# Revit family: HVAC_Water-Heaters_Enertech_CTC-EcoAir-510M
name_source: partatom
category: Specialty Equipment
revit_build: Autodesk Revit 2017 (Build: 20190508_0315(x64)
units: mm (PartAtom-declared; Revit-internal decimal feet)

## family parameters
Always vertical = Yes
Cut with Voids When Loaded = No
OmniClass Number = 23.75.00.00
OmniClass Title = Climate Control (HVAC)
Part Type = Normal
Room Calculation Point = No
Round Connector Dimension = Use Diameter
Shared = No
Work Plane-Based = No

## types (1)
- CTC EcoAir 510M - 230V1N
    AirFlow = 2350 m3/h
    AssetType = Fixed
    BIMObjectName = HVAC_Water-Heaters_Enertech_CTC-EcoAir-510M
    Brand = CTC
    BrineSystem_Min_MaxPressure = 0.2 - 3.0 bar
    CO2Equivalent = 4.594 tonnes
    COP = 4.67
    Capacity = Variable
    Category = Heat Pumps, Air-to-water
    Color = grey
    ConvergoRefNr = 0091-1710-0002-SE
    Cost = 0 $
    Description = The CTC EcoAir 510M is a variable-speed heat pump with an output of 2-10 kW that automatically adapts to the building's output requirements during the year. Model: 510M
    DurationUnit = Year
    EnergyClassHeatingWithControl = A+++ / A++
    EnergyClassHeatingWithoutControl = A++ / A++
    GroupFuse = 25 A
    HasProtectiveEarth = Yes
    IP_Code = IP X4
    IfcExportAs = IfcElectricalDeviceCommon
    IfcExportType = HEATER
    InPutPower = 0.54 kW
    Manufacturer = Enertech AB
    ManufacturerCountry = Sweden
    ManufacturerName = Enertech AB
    ManufacturerURL = https://ctc.se
    Material = Steel/copper
    MaxAirFlowRate = 3800 m3/h
    MaxOperatingPressureThermalStore = 3 bar
    MaxStartingCurrent = 2.8 A
    Model = CTC EcoAir 510M
    ModelNumber = 587601001
    NBSDescription = Air to water heat pumps
    NBSReference = 90-40-40/320
    Name = CTC-EcoAir-510M
    NominalCurrent = 0 A
    NominalDepth = 545 mm
    NominalFrequencyRange = 50 Hz
    NominalHeight = 1080 mm  [stored 3.54331 ft]
    NominalVoltage = 230 V
    NominalWidth = 1245 mm
    NumberOfPoles = 1
    OutputRange = 2-10 kW
    PhaseAngle = 0.00°
    PowerFactor = 0 W
    ProductInformation = The CTC EcoAir 510M is a variable-speed heat pump with an output of 2-10 kW that automatically adapts to the building's output requirements during the year. Model: 510M
    PumpMainMaterial = Stainless Steel
    RatedCurrent = 21 A
    RatedHeatOutputModerate = 4 kW
    RatedVoltage = 230 V
    RefrigerantQuantity = 2.8 kg
    RefrigerantType = R410A
    Revision = 4
    SCOPCold = 3.9
    SCOPModerate = 4.3
    SCOPWarm = 5.5
    Shape = Rectangular
    Size = 545x1245x1080 mm
    Sound pressureLPA 10m = 33 dB
    Sound pressureLPA 5m = 40 dB
    SoundPowerLWA = 59.7 dB
    SpecifiedOutput = 2.52 kW
    Touchscreen = no
    UNSPSCCode = 40101806
    URL = https://ctc-heating.com
    Uniclass2 = Pr_40_70_65
    Uniclass2015Description = Preparation catering equipment
    Uniclass2015Reference = Pr_40_70_65
    UsageCurrent = 0 A
    Version = 1
    VersionDate = 10/11/2020
    WarrantyDurationUnit = Year
    WaterVolumeHeathingSystem = 1.9 liters
    Weight = 119 kg

note: [stored X ft] marks values corroborated as IEEE doubles in the binary element streams (Revit-internal decimal feet)

## geometry (parser evidence)
native form markers: Sweep x6
no freeform markers — native parametric forms only
